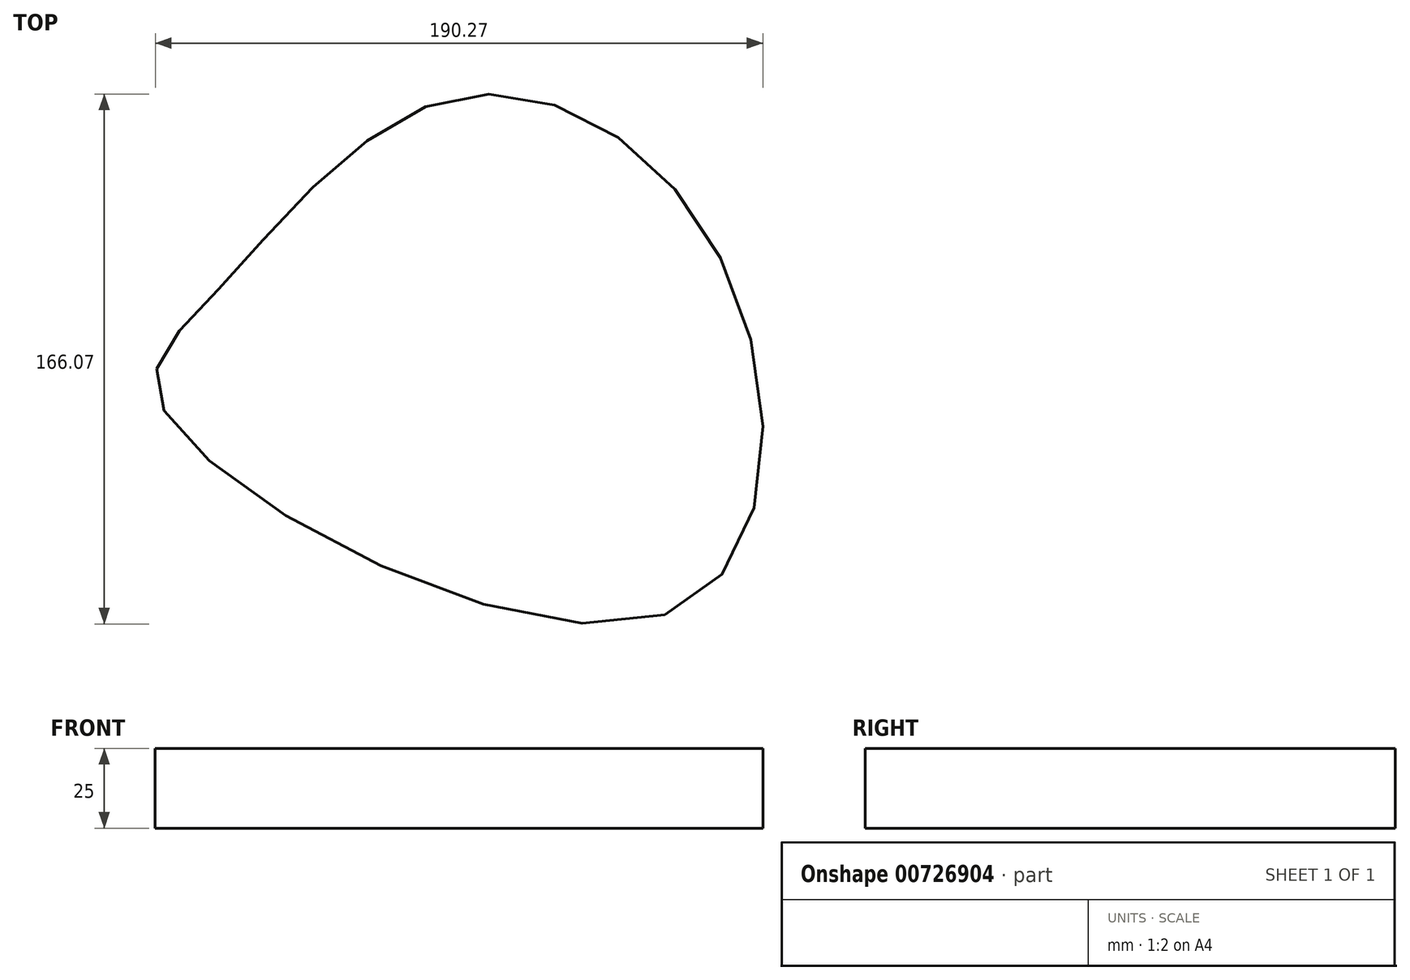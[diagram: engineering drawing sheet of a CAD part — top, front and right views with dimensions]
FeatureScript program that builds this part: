
annotation { "Feature Type Name" : "Feature", "Feature Type Description" : "" }
export const myFeature = defineFeature(function(context is Context, id is Id, definition is map)
    precondition{}
    {
        {
            var Q0;
            Q0=qCreatedBy(makeId("Top.planeOp"),FACE);
            var sketch = newSketch(context, id + "F0", { "sketchPlane" : qUnion([Q0])});
            skFitSpline(sketch, "E0", {"points": [v(-136.25, 0) * mm, v(-120.01, 37.08) * mm, v(-44.54, 98.07) * mm, v(39.27, 45.42) * mm, v(21.28, -63.85) * mm, v(-136.25, 0) * mm]});
            skSolve(sketch);
        }
        {
            var Q0;
            Q0=makeQuery(id+"F0.imprint","IMPRINT",FACE,{"disambiguationData":[TD([[makeQuery(id+"F0.imprint","IMPRINT",EDGE,{"derivedFrom":sQuery(id+"F0.wireOp",EDGE,"E0")}),-1.0]])]});
            extrude(context, id + "F1", {"entities" : qUnion([Q0]), "depth" : 25 * mm, "offsetDistance" : 25 * mm});
        }
    });
